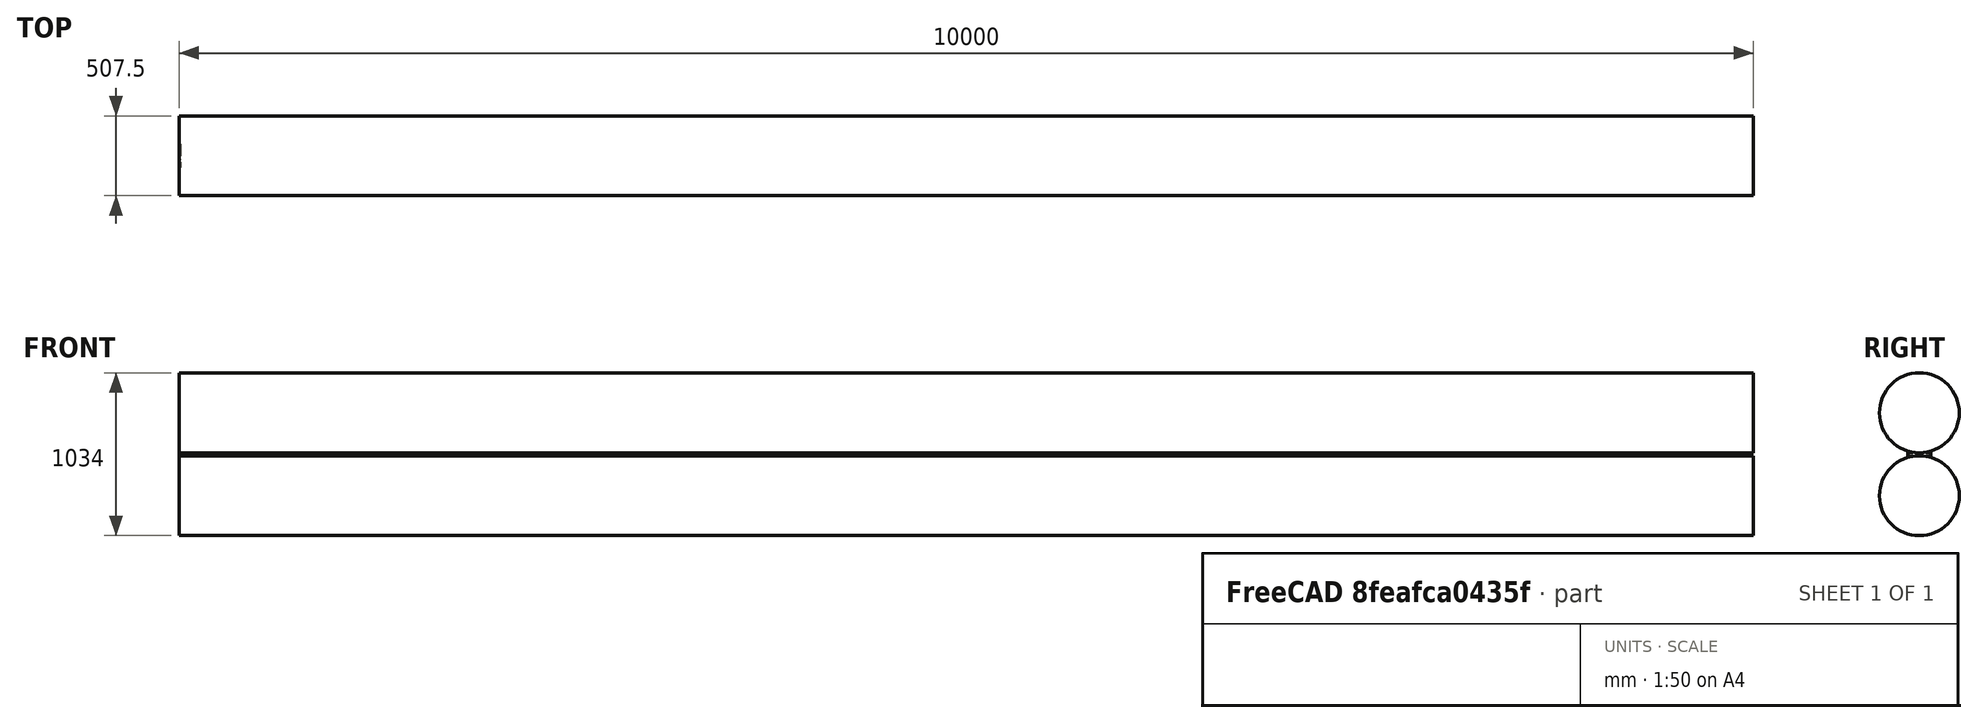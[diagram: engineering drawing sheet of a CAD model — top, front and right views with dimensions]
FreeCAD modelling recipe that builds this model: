
FCSTD DOCUMENT  (FreeCAD 0.16R)
Label: Thermos-Handle
License: All rights reserved
LicenseURL: http://en.wikipedia.org/wiki/All_rights_reserved
objects: Sketcher::SketchObject×5, PartDesign::Fillet×5, PartDesign::Pocket×4, PartDesign::LinearPattern×3, PartDesign::Pad×1, Mesh::Feature×1
note: 23 computed .brp shape members not serialized (recipe doc carries the construction recipe); baked Part::Feature solids carry a one-line shape summary decoded from their .brp

FEATURE [Sketcher::SketchObject] Sketch
  sketch-geometry (4):
    g0: LineSegment StartX=-5 StartY=74 StartZ=0 EndX=5 EndY=74 EndZ=0
    g1: LineSegment StartX=5 StartY=74 StartZ=0 EndX=5 EndY=-74 EndZ=0
    g2: LineSegment StartX=5 StartY=-74 StartZ=0 EndX=-5 EndY=-74 EndZ=0
    g3: LineSegment StartX=-5 StartY=-74 StartZ=0 EndX=-5 EndY=74 EndZ=0
  constraints (11):
    c: Coincident(g0,g1)
    c: Coincident(g1,g2)
    c: Coincident(g2,g3)
    c: Coincident(g3,g0)
    c: Horizontal(g0)
    c: Horizontal(g2)
    c: Vertical(g1)
    c: Vertical(g3)
    c: Symmetric(g1,g0,g-1)
    c: DistanceY(g1,g1) = 148
    c: DistanceX(g2,g2) = 10
FEATURE [PartDesign::Pad] Pad
  Length = 26
  Length2 = 100
  Sketch = -> Sketch
  Type = 0
FEATURE [Sketcher::SketchObject] Sketch001
  ExternalGeometry = -> [Pad]
  Placement = pos=(0,0,0) rot=(1,0,0;3.14159rad)
  Support = -> Pad [Face5]
  sketch-geometry (8):
    g0: GeomPoint [constr] X=5 Y=-47 Z=0
    g1: GeomPoint [constr] X=5 Y=-25 Z=0
    g2: GeomPoint [constr] X=1 Y=-36 Z=0
    g3: LineSegment [constr] StartX=5 StartY=-25 StartZ=0 EndX=1 EndY=-36 EndZ=0
    g4: LineSegment [constr] StartX=1 StartY=-36 StartZ=0 EndX=5 EndY=-47 EndZ=0
    g5: ArcOfCircle CenterX=18.125 CenterY=-36 CenterZ=0 NormalX=0 NormalY=0 NormalZ=1 Radius=17.125 StartAngle=2.42606 EndAngle=3.85712
    g6: LineSegment StartX=5.2 StartY=-24.7657 StartZ=0 EndX=18.125 EndY=-36 EndZ=0
    g7: LineSegment StartX=18.125 StartY=-36 StartZ=0 EndX=5.2 EndY=-47.2343 EndZ=0
  constraints (19):
    c: PointOnObject(g0,g-3)
    c: PointOnObject(g1,g-3)
    c: DistanceY(g0,g1) = 22
    c: DistanceY(g-1,g0) = -47
    c: Coincident(g3,g1)
    c: Coincident(g3,g2)
    c: Coincident(g4,g2)
    c: Coincident(g4,g0)
    c: Equal(g4,g3)
    c: DistanceX(g-2,g2) = 1
    c: PointOnObject(g1,g5)
    c: PointOnObject(g2,g5)
    c: PointOnObject(g0,g5)
    c: Coincident(g6,g5)
    c: Coincident(g6,g5)
    c: Coincident(g7,g5)
    c: Coincident(g7,g5)
    c: DistanceX(g1,g5) = 0.2
    c: DistanceX(g5,g5) = 0
FEATURE [PartDesign::Pocket] Pocket
  Length = 5
  Sketch = -> Sketch001
  Type = 1
FEATURE [PartDesign::LinearPattern] LinearPattern
  Direction = -> Sketch001 [V_Axis]
  Length = 72
  Occurrences = 4
  Originals = -> [Pocket]
FEATURE [Sketcher::SketchObject] Sketch002
  ExternalGeometry = -> [LinearPattern]
  Placement = pos=(-5,0,0) rot=(0.57735,-0.57735,-0.57735;2.0944rad)
  Support = -> LinearPattern [Face2]
  sketch-geometry (10):
    g0: Circle CenterX=0 CenterY=276.25 CenterZ=0 NormalX=0 NormalY=0 NormalZ=1 Radius=253.75
    g1: GeomPoint [constr] X=0 Y=22.5 Z=0
    g2: GeomPoint [constr] X=-42 Y=26 Z=0
    g3: GeomPoint [constr] X=42 Y=26 Z=0
    g4: Circle CenterX=0 CenterY=-250.25 CenterZ=0 NormalX=0 NormalY=0 NormalZ=1 Radius=253.75
    g5: GeomPoint [constr] X=0 Y=3.5 Z=0
    g6: GeomPoint [constr] X=42 Y=0 Z=0
    g7: GeomPoint [constr] X=-42 Y=0 Z=0
    g8: LineSegment [constr] StartX=0 StartY=22.5 StartZ=0 EndX=0 EndY=26 EndZ=0
    g9: LineSegment [constr] StartX=0 StartY=3.5 StartZ=0 EndX=0 EndY=0 EndZ=0
  constraints (23):
    c: PointOnObject(g0,g-2)
    c: PointOnObject(g1,g0)
    c: PointOnObject(g1,g-2)
    c: PointOnObject(g2,g0)
    c: PointOnObject(g3,g0)
    c: PointOnObject(g3,g-3)
    c: PointOnObject(g2,g-3)
    c: PointOnObject(g4,g-2)
    c: PointOnObject(g5,g4)
    c: PointOnObject(g6,g4)
    c: PointOnObject(g7,g4)
    c: PointOnObject(g7,g-1)
    c: PointOnObject(g6,g-1)
    c: DistanceY(g5,g1) = 19
    c: DistanceX(g2,g7) = 0
    c: DistanceX(g2,g3) = 84
    c: PointOnObject(g5,g-2)
    c: Coincident(g8,g1)
    c: PointOnObject(g8,g-3)
    c: Vertical(g8)
    c: Coincident(g9,g5)
    c: Coincident(g9,g-1)
    c: Equal(g9,g8)
FEATURE [PartDesign::Pocket] Pocket001
  Length = 5
  Sketch = -> Sketch002
  Type = 1
FEATURE [Sketcher::SketchObject] Sketch004
  Placement = pos=(0,0,26) rot=(0,0,1;0rad)
  Support = -> Pocket001 [Face9]
  sketch-geometry (4):
    g0: LineSegment StartX=-1 StartY=70 StartZ=0 EndX=2 EndY=70 EndZ=0
    g1: LineSegment StartX=2 StartY=70 StartZ=0 EndX=2 EndY=47 EndZ=0
    g2: LineSegment StartX=2 StartY=47 StartZ=0 EndX=-1 EndY=47 EndZ=0
    g3: LineSegment StartX=-1 StartY=47 StartZ=0 EndX=-1 EndY=70 EndZ=0
  constraints (12):
    c: Coincident(g0,g1)
    c: Coincident(g1,g2)
    c: Coincident(g2,g3)
    c: Coincident(g3,g0)
    c: Horizontal(g0)
    c: Horizontal(g2)
    c: Vertical(g1)
    c: Vertical(g3)
    c: DistanceX(g2,g2) = 3
    c: DistanceY(g1,g1) = 23
    c: DistanceX(g2) = -1
    c: DistanceY(g0) = 70
FEATURE [PartDesign::Pocket] Pocket002
  Length = 5
  Sketch = -> Sketch004
  Type = 1
FEATURE [PartDesign::LinearPattern] LinearPattern001
  Direction = -> Sketch004 [V_Axis]
  Length = 117
  Occurrences = 2
  Originals = -> [Pocket002]
  Reversed = true
FEATURE [Sketcher::SketchObject] Sketch003
  ExternalGeometry = -> [Pocket001]
  Placement = pos=(-5,0,0) rot=(0.57735,-0.57735,-0.57735;2.0944rad)
  Support = -> LinearPattern001 [Face2]
  sketch-geometry (8):
    g0: Circle CenterX=74 CenterY=-79.0682 CenterZ=0 NormalX=0 NormalY=0 NormalZ=1 Radius=84.5682
    g1: Circle CenterX=74 CenterY=105.068 CenterZ=0 NormalX=0 NormalY=0 NormalZ=1 Radius=84.5682
    g2: GeomPoint [constr] X=44 Y=26 Z=0
    g3: GeomPoint [constr] X=44 Y=0 Z=0
    g4: LineSegment [constr] StartX=44 StartY=26 StartZ=0 EndX=44 EndY=0 EndZ=0
    g5: GeomPoint [constr] X=74 Y=20.5 Z=0
    g6: GeomPoint [constr] X=74 Y=5.5 Z=0
    g7: LineSegment [constr] StartX=74 StartY=20.5 StartZ=0 EndX=74 EndY=5.5 EndZ=0
  constraints (18):
    c: PointOnObject(g2,g1)
    c: PointOnObject(g2,g-3)
    c: PointOnObject(g3,g0)
    c: PointOnObject(g3,g-1)
    c: Coincident(g4,g2)
    c: Coincident(g4,g3)
    c: Vertical(g4)
    c: DistanceX(g-3,g2) = 2
    c: PointOnObject(g5,g1)
    c: PointOnObject(g6,g0)
    c: Coincident(g7,g5)
    c: Coincident(g7,g6)
    c: Vertical(g7)
    c: DistanceY(g7,g7) = 15
    c: DistanceX(g2,g5) = 30
    c: DistanceX(g1,g5) = 0
    c: DistanceX(g0,g6) = 0
    c: Equal(g1,g0)
FEATURE [PartDesign::Pocket] Pocket003
  Length = 5
  Sketch = -> Sketch003
  Type = 1
FEATURE [PartDesign::LinearPattern] LinearPattern002
  Direction = -> Sketch003 [H_Axis]
  Length = 148
  Occurrences = 2
  Originals = -> [Pocket003]
  Reversed = true
FEATURE [PartDesign::Fillet] Fillet
  Base = -> LinearPattern002 [Edge2,Edge4,Edge29,Edge68]
  Radius = 4
FEATURE [PartDesign::Fillet] Fillet001
  Base = -> Fillet [Edge90,Edge89,Edge88,Edge87,Edge86,Edge85,Edge41,Edge38,Edge37,Edge7,Edge56,Edge54,Edge74,Edge57,Edge47,Edge20]
  Radius = 2
FEATURE [PartDesign::Fillet] Fillet002
  Base = -> Fillet001 [Edge19]
  Radius = 1.5
FEATURE [PartDesign::Fillet] Fillet003
  Base = -> Fillet002 [Edge64]
  Radius = 1.5
FEATURE [PartDesign::Fillet] Fillet004
  Base = -> Fillet003 [Edge190,Edge188,Edge191,Edge189,Edge299,Edge301,Edge298,Edge300]
  Radius = 1
FEATURE [Mesh::Feature] Mesh  label="Fillet004 (Meshed)"
